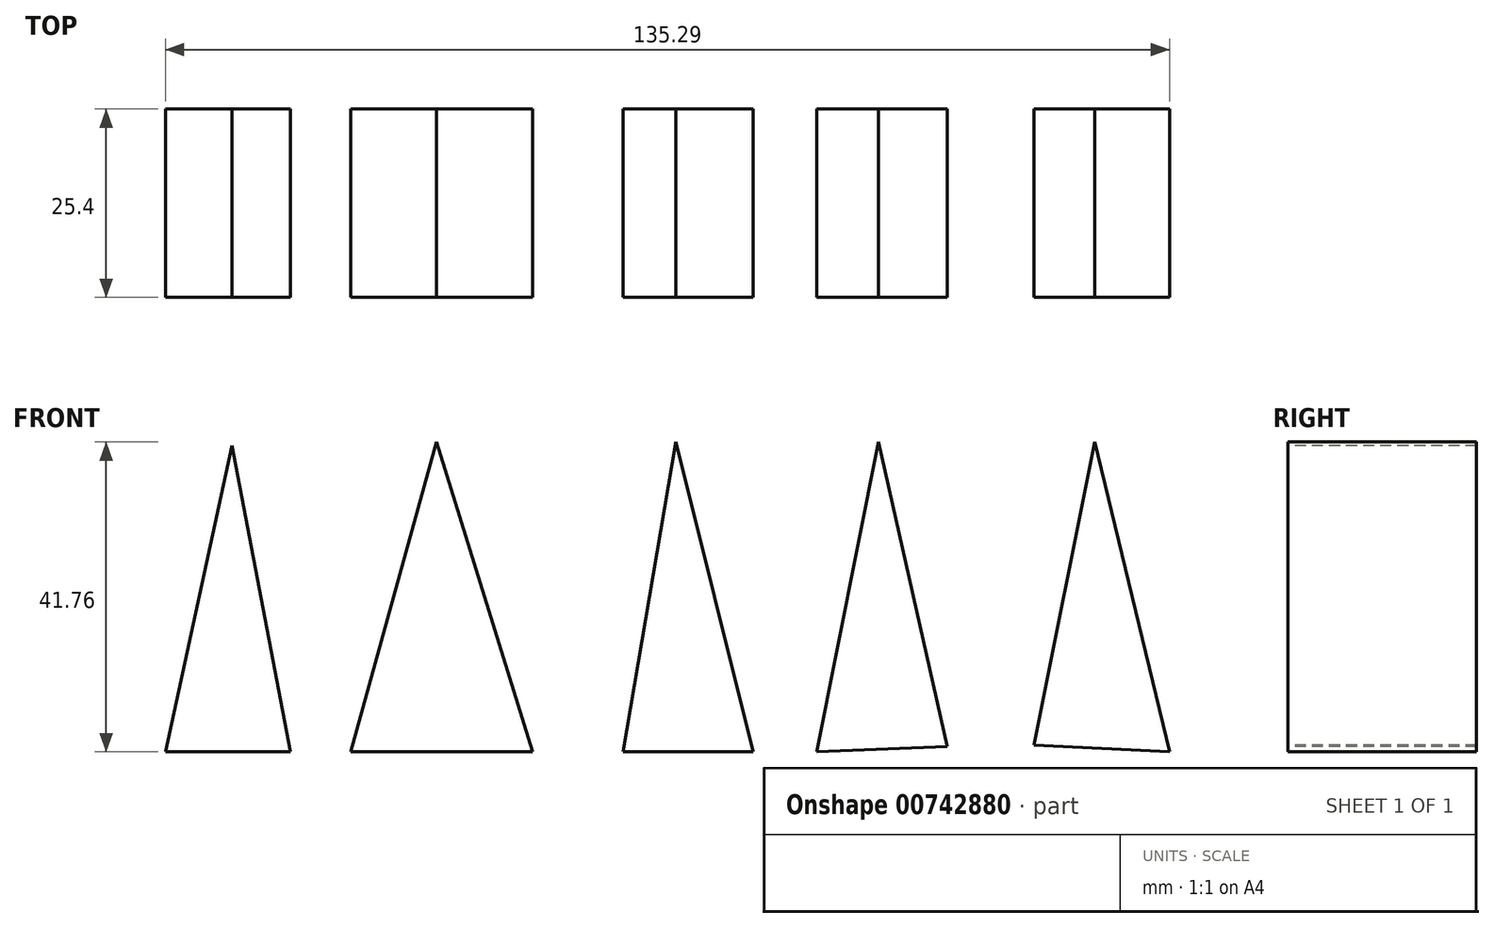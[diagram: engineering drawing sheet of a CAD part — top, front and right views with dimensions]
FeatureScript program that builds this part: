
annotation { "Feature Type Name" : "Feature", "Feature Type Description" : "" }
export const myFeature = defineFeature(function(context is Context, id is Id, definition is map)
    precondition{}
    {
        {
            var Q0;
            Q0=qCreatedBy(makeId("Front.planeOp"),FACE);
            var sketch = newSketch(context, id + "F0", { "sketchPlane" : qUnion([Q0])});
            skLineSegment(sketch, "E0", {"start": v(-72, 0) * mm, "end": v(-68.8, 0) * mm});
            skLineSegment(sketch, "E1", {"start": v(-68.8, 0) * mm, "end": v(-59.82, 41.28) * mm});
            skLineSegment(sketch, "E2", {"start": v(-59.82, 41.28) * mm, "end": v(-51.99, 0) * mm});
            skLineSegment(sketch, "E3", {"start": v(-51.99, 0) * mm, "end": v(-46.77, 0) * mm});
            skLineSegment(sketch, "E4", {"start": v(-46.77, 0) * mm, "end": v(-43.82, 0) * mm});
            skLineSegment(sketch, "E5", {"start": v(-43.82, 0) * mm, "end": v(-32.28, 41.76) * mm});
            skLineSegment(sketch, "E6", {"start": v(-32.28, 41.76) * mm, "end": v(-19.36, 0) * mm});
            skLineSegment(sketch, "E7", {"start": v(-19.36, 0) * mm, "end": v(-12.9, 0) * mm});
            skLineSegment(sketch, "E8", {"start": v(-12.9, 0) * mm, "end": v(-7.13, 0) * mm});
            skLineSegment(sketch, "E9", {"start": v(-7.13, 0) * mm, "end": v(0, 41.76) * mm});
            skLineSegment(sketch, "E10", {"start": v(0, 41.76) * mm, "end": v(10.41, 0) * mm});
            skLineSegment(sketch, "E11", {"start": v(10.41, 0) * mm, "end": v(14.34, 0) * mm});
            skLineSegment(sketch, "E12", {"start": v(14.34, 0) * mm, "end": v(18.95, 0) * mm});
            skLineSegment(sketch, "E13", {"start": v(18.95, 0) * mm, "end": v(27.26, 41.76) * mm});
            skLineSegment(sketch, "E14", {"start": v(27.26, 41.76) * mm, "end": v(36.72, 0) * mm});
            skLineSegment(sketch, "E15", {"start": v(36.72, 0) * mm, "end": v(40.5, 0.86) * mm});
            skLineSegment(sketch, "E16", {"start": v(40.5, 0.86) * mm, "end": v(48.26, 0.86) * mm});
            skLineSegment(sketch, "E17", {"start": v(48.26, 0.86) * mm, "end": v(56.4, 41.76) * mm});
            skLineSegment(sketch, "E18", {"start": v(56.4, 41.76) * mm, "end": v(66.49, 0) * mm});
            skLineSegment(sketch, "E19", {"start": v(66.49, 0) * mm, "end": v(70.03, 0.86) * mm});
            skLineSegment(sketch, "E20", {"start": v(-68.8, 0) * mm, "end": v(-51.99, 0) * mm});
            skLineSegment(sketch, "E21", {"start": v(-19.36, 0) * mm, "end": v(-43.82, 0) * mm});
            skLineSegment(sketch, "E22", {"start": v(-7.13, 0) * mm, "end": v(18.95, 0) * mm});
            skLineSegment(sketch, "E23", {"start": v(40.5, 0.86) * mm, "end": v(18.95, 0) * mm});
            skLineSegment(sketch, "E24", {"start": v(48.26, 0.86) * mm, "end": v(66.49, 0) * mm});
            skSolve(sketch);
        }
        {
            var Q0;
            Q0=makeQuery(id+"F0.imprint","IMPRINT",FACE,{"disambiguationData":[TD([[makeQuery(id+"F0.imprint","IMPRINT",EDGE,{"derivedFrom":sQuery(id+"F0.wireOp",EDGE,"E1")}),-1.0]])]});
            var Q1;
            Q1=makeQuery(id+"F0.imprint","IMPRINT",FACE,{"disambiguationData":[TD([[makeQuery(id+"F0.imprint","IMPRINT",EDGE,{"derivedFrom":sQuery(id+"F0.wireOp",EDGE,"E5")}),-1.0]])]});
            var Q2;
            {var subQ0=sQuery(id+"F0.wireOp",EDGE,"E9");Q2=makeQuery(id+"F0.imprint","IMPRINT",FACE,{"disambiguationData":[TD([[makeQuery(id+"F0.imprint","IMPRINT",EDGE,{"derivedFrom":subQ0}),-1.0]])]});}
            var Q3;
            {var subQ0=sQuery(id+"F0.wireOp",EDGE,"E13");Q3=makeQuery(id+"F0.imprint","IMPRINT",FACE,{"disambiguationData":[TD([[makeQuery(id+"F0.imprint","IMPRINT",EDGE,{"derivedFrom":subQ0}),-1.0]])]});}
            var Q4;
            Q4=makeQuery(id+"F0.imprint","IMPRINT",FACE,{"disambiguationData":[TD([[makeQuery(id+"F0.imprint","IMPRINT",EDGE,{"derivedFrom":sQuery(id+"F0.wireOp",EDGE,"E17")}),-1.0]])]});
            extrude(context, id + "F1", {"entities" : qUnion([Q0, Q1, Q2, Q3, Q4]), "oppositeDirection" : true, "depth" : 25.4 * mm, "offsetDistance" : 25.4 * mm});
        }
    });
